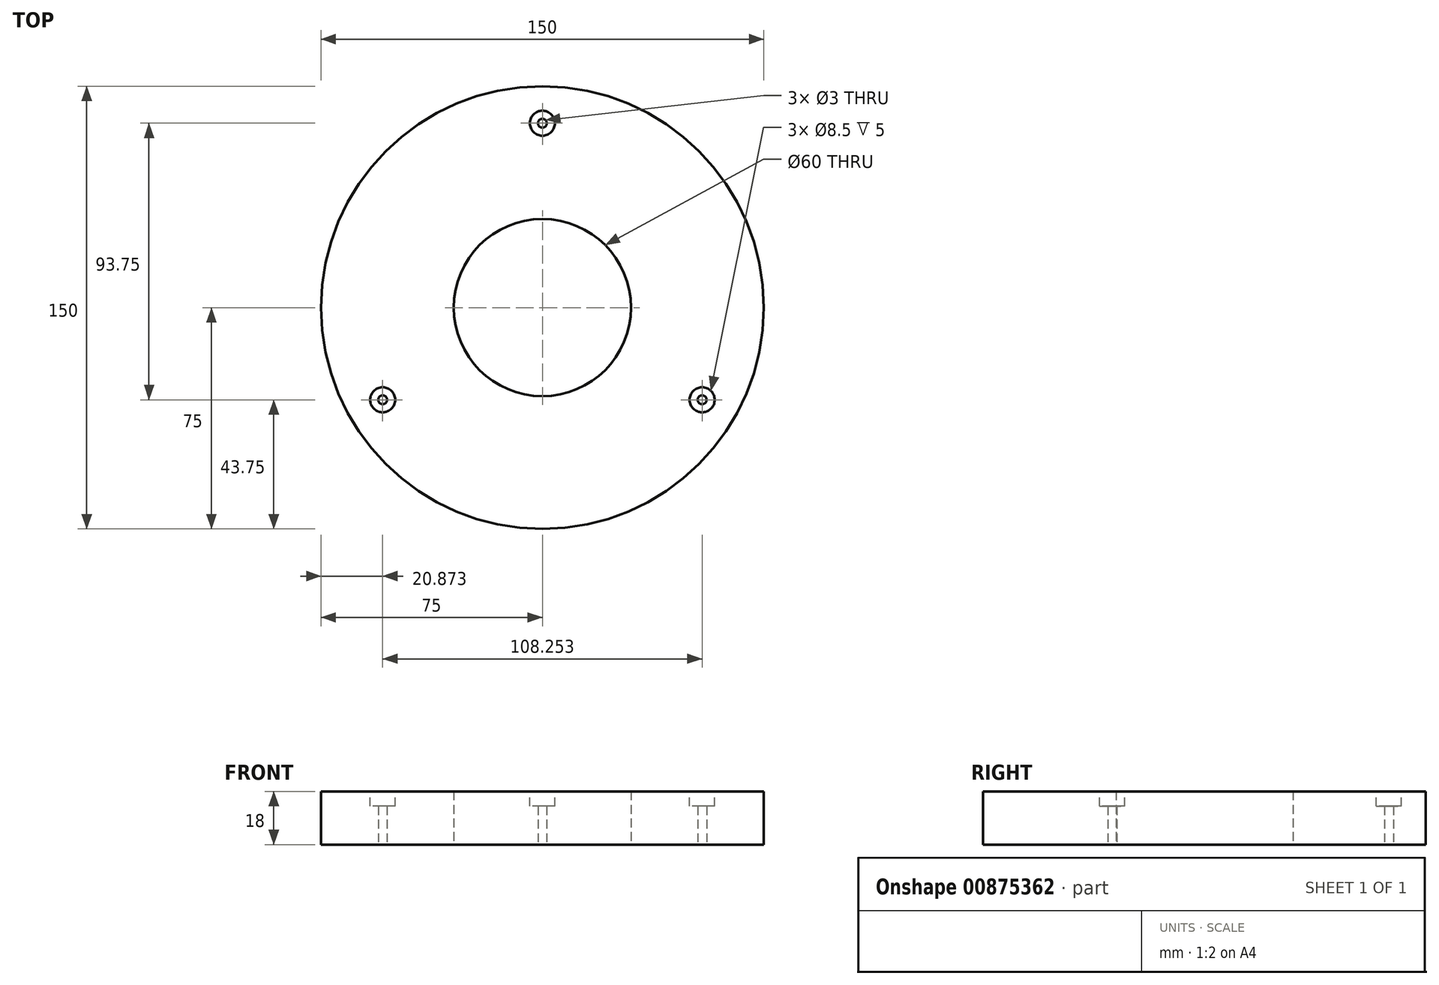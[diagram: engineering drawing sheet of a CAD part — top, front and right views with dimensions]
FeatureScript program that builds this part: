
annotation { "Feature Type Name" : "Feature", "Feature Type Description" : "" }
export const myFeature = defineFeature(function(context is Context, id is Id, definition is map)
    precondition{}
    {
        {
            var Q0;
            Q0=qCreatedBy(makeId("Top.planeOp"),FACE);
            var sketch = newSketch(context, id + "F0", { "sketchPlane" : qUnion([Q0])});
            skCircle(sketch, "E0", {"center": v(0, 0) * mm, "radius": 75 * mm});
            skCircle(sketch, "E1", {"center": v(0, 0) * mm, "radius": 62.5 * mm, "construction": true});
            skLineSegment(sketch, "E2", {"start": v(111.84, 0) * mm, "end": v(-118.89, 0) * mm, "construction": true});
            skLineSegment(sketch, "E3", {"start": v(0, -136.53) * mm, "end": v(0, 174.78) * mm, "construction": true});
            skCircle(sketch, "E4", {"center": v(0, 62.5) * mm, "radius": 1.5 * mm});
            skCircle(sketch, "E5.1.0", {"center": v(-54.13, -31.25) * mm, "radius": 1.5 * mm});
            skCircle(sketch, "E5.2.0", {"center": v(54.13, -31.25) * mm, "radius": 1.5 * mm});
            skCircle(sketch, "E6", {"center": v(0, 0) * mm, "radius": 30 * mm});
            skSolve(sketch);
        }
        {
            var Q0;
            Q0=makeQuery(id+"F0.imprint","IMPRINT",FACE,{"disambiguationData":[TD([[makeQuery(id+"F0.imprint","IMPRINT",EDGE,{"derivedFrom":sQuery(id+"F0.wireOp",EDGE,"E0")}),1.0]])]});
            extrude(context, id + "F1", {"entities" : qUnion([Q0]), "depth" : 18 * mm, "offsetDistance" : 25 * mm});
        }
        {
            var Q0;
            Q0=makeQuery(id+"F1.opExtrude","CAP_FACE",FACE,{"disambiguationData":[OSD([sQuery(id+"F0.wireOp",EDGE,"E0"),sQuery(id+"F0.wireOp",EDGE,"E4"),sQuery(id+"F0.wireOp",EDGE,"E5.1.0"),sQuery(id+"F0.wireOp",EDGE,"E5.2.0"),sQuery(id+"F0.wireOp",EDGE,"E6")])],"isStart":false});
            var sketch = newSketch(context, id + "F2", { "sketchPlane" : qUnion([Q0])});
            skCircle(sketch, "E7", {"center": v(-54.13, -31.25) * mm, "radius": 4.25 * mm});
            skCircle(sketch, "E8.1.0", {"center": v(54.13, -31.25) * mm, "radius": 4.25 * mm});
            skCircle(sketch, "E8.2.0", {"center": v(0, 62.5) * mm, "radius": 4.25 * mm});
            skPoint(sketch, "E8.center", {"position": v(0, 0) * mm});
            skSolve(sketch);
        }
        {
            var Q0;
            Q0 = qSketchRegion(id + "F2", true);
            extrude(context, id + "F3", {"entities" : qUnion([Q0]), "operationType" : NewBodyOperationType.REMOVE, "oppositeDirection" : true, "depth" : 5 * mm, "offsetDistance" : 25 * mm});
        }
    });
